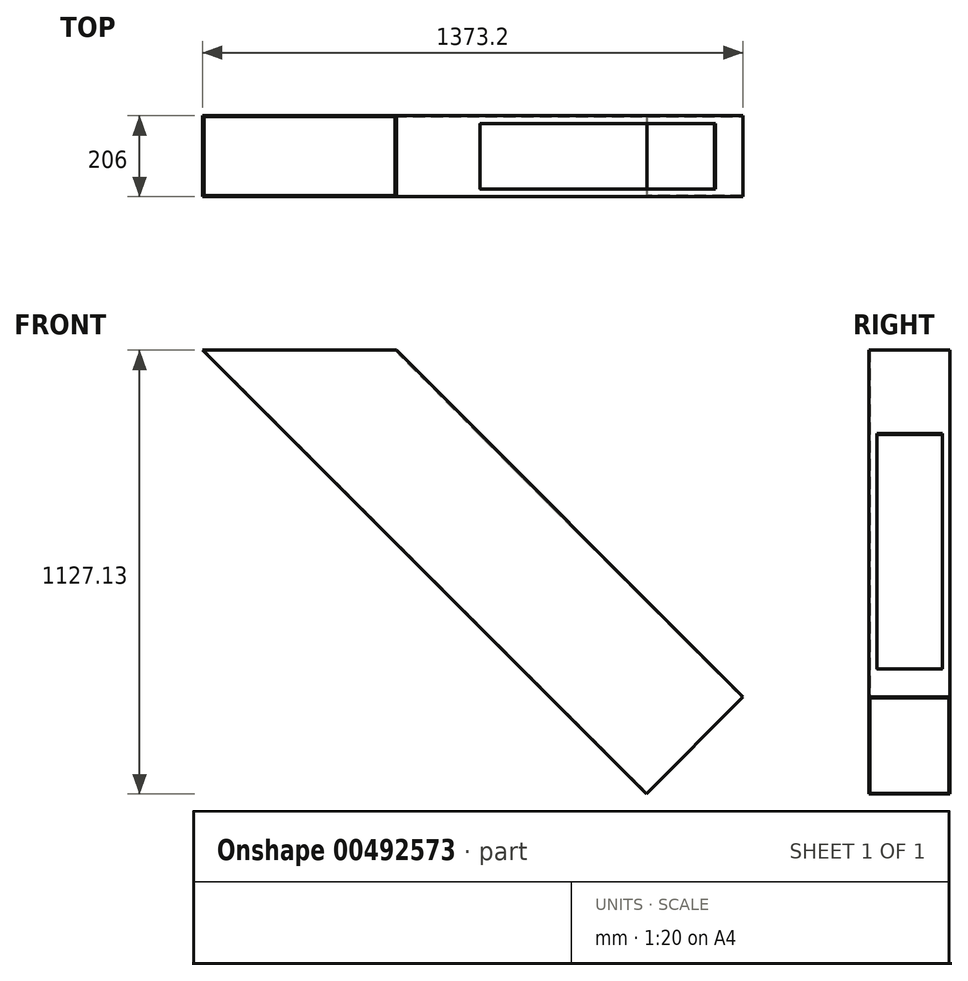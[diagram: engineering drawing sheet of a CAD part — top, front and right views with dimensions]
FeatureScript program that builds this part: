
annotation { "Feature Type Name" : "Feature", "Feature Type Description" : "" }
export const myFeature = defineFeature(function(context is Context, id is Id, definition is map)
    precondition{}
    {
        {
            var Q0;
            Q0=qCreatedBy(makeId("Right.planeOp"),FACE);
            var Q1;
            Q1=qCreatedBy(makeId("Top.planeOp"),FACE);
            cPlane(context, id + "F0", {"entities" : qUnion([Q0, Q1]), "cplaneType" : CPlaneType.MID_PLANE, "offset" : 25 * mm, "width" : 150 * mm, "height" : 150 * mm});
        }
        {
            var Q0;
            Q0=qCreatedBy(makeId("Front.planeOp"),FACE);
            var sketch = newSketch(context, id + "F1", { "sketchPlane" : qUnion([Q0])});
            skLineSegment(sketch, "E0", {"start": v(0, 0) * mm, "end": v(62.48, 36.07) * mm, "construction": true});
            skPoint(sketch, "E1", {"position": v(62.48, 36.07) * mm});
            skSolve(sketch);
        }
        {
            var Q0;
            Q0=qCreatedBy(makeId("Top.planeOp"),FACE);
            var Q1;
            Q1=sQuery(id+"F1.wireOp",EDGE,"E0");
            cPlane(context, id + "F2", {"entities" : qUnion([Q0, Q1]), "cplaneType" : CPlaneType.LINE_ANGLE, "offset" : 25 * mm, "angle" : 0 * degree, "width" : 150 * mm, "height" : 150 * mm});
        }
        {
            var Q0;
            Q0=qCreatedBy(id+"F0.planeOp",FACE);
            cPlane(context, id + "F3", {"entities" : qUnion([Q0]), "cplaneType" : CPlaneType.OFFSET, "offset" : 1420 * mm, "width" : 150 * mm, "height" : 150 * mm});
        }
        {
            var Q0;
            Q0=qCreatedBy(id+"F3.planeOp",FACE);
            var sketch = newSketch(context, id + "F4", { "sketchPlane" : qUnion([Q0])});
            skLineSegment(sketch, "E2.bottom", {"start": v(103, 174) * mm, "end": v(-103, 174) * mm});
            skLineSegment(sketch, "E2.top", {"start": v(103, -174) * mm, "end": v(-103, -174) * mm});
            skLineSegment(sketch, "E2.left", {"start": v(103, 174) * mm, "end": v(103, -174) * mm});
            skLineSegment(sketch, "E2.right", {"start": v(-103, 174) * mm, "end": v(-103, -174) * mm});
            skPoint(sketch, "E2.middle", {"position": v(0, 0) * mm});
            skSolve(sketch);
        }
        {
            var Q0;
            Q0 = qSketchRegion(id + "F4", true);
            extrude(context, id + "F5", {"entities" : qUnion([Q0]), "oppositeDirection" : true, "depth" : 1800 * mm, "offsetDistance" : 25 * mm});
        }
        {
            var Q0;
            Q0=makeQuery(id+"F5.opExtrude","CAP_FACE",FACE,{"disambiguationData":[OSD([sQuery(id+"F4.wireOp",EDGE,"E2.bottom"),sQuery(id+"F4.wireOp",EDGE,"E2.top"),sQuery(id+"F4.wireOp",EDGE,"E2.left"),sQuery(id+"F4.wireOp",EDGE,"E2.right")])],"isStart":true});
            shell(context, id + "F6", {"entities" : qUnion([Q0]), "thickness" : 2.5 * mm});
        }
        {
            var Q0;
            Q0=qCreatedBy(makeId("Top.planeOp"),FACE);
            var sketch = newSketch(context, id + "F7", { "sketchPlane" : qUnion([Q0])});
            skLineSegment(sketch, "E3.bottom", {"start": v(-491.61, 279.81) * mm, "end": v(570.76, 279.81) * mm});
            skLineSegment(sketch, "E3.top", {"start": v(-491.61, -320.2) * mm, "end": v(570.76, -320.2) * mm});
            skLineSegment(sketch, "E3.left", {"start": v(-491.61, 279.81) * mm, "end": v(-491.61, -320.2) * mm});
            skLineSegment(sketch, "E3.right", {"start": v(570.76, 279.81) * mm, "end": v(570.76, -320.2) * mm});
            skSolve(sketch);
        }
        {
            var Q0;
            Q0=makeQuery(id+"F7.imprint","IMPRINT",FACE,{"disambiguationData":[TD([[makeQuery(id+"F7.imprint","IMPRINT",EDGE,{"derivedFrom":sQuery(id+"F7.wireOp",EDGE,"E3.bottom")}),-1.0]])]});
            extrude(context, id + "F8", {"entities" : qUnion([Q0]), "operationType" : NewBodyOperationType.REMOVE, "endBound" : BoundingType.THROUGH_ALL, "depth" : 25 * mm, "offsetDistance" : 25 * mm});
        }
        {
            var Q0;
            Q0=makeQuery(id+"F5.opExtrude","SWEPT_FACE",FACE,{"disambiguationData":[OSD([sQuery(id+"F4.wireOp",EDGE,"E2.bottom")])]});
            var sketch = newSketch(context, id + "F9", { "sketchPlane" : qUnion([Q0])});
            skLineSegment(sketch, "E4", {"start": v(0, -1593.28) * mm, "end": v(0, -174) * mm, "construction": true});
            skPoint(sketch, "E4.startSnap0", {"position": v(0, -1420) * mm});
            skLineSegment(sketch, "E5.bottom", {"start": v(83, -1320) * mm, "end": v(-83, -1320) * mm});
            skLineSegment(sketch, "E5.top", {"start": v(83, -474) * mm, "end": v(-83, -474) * mm});
            skLineSegment(sketch, "E5.left", {"start": v(83, -1320) * mm, "end": v(83, -474) * mm});
            skLineSegment(sketch, "E5.right", {"start": v(-83, -1320) * mm, "end": v(-83, -474) * mm});
            skSolve(sketch);
        }
        {
            var Q0;
            Q0 = qSketchRegion(id + "F9", true);
            extrude(context, id + "F10", {"entities" : qUnion([Q0]), "operationType" : NewBodyOperationType.REMOVE, "endBound" : BoundingType.SYMMETRIC, "oppositeDirection" : true, "depth" : 25 * mm, "offsetDistance" : 25 * mm});
        }
    });
